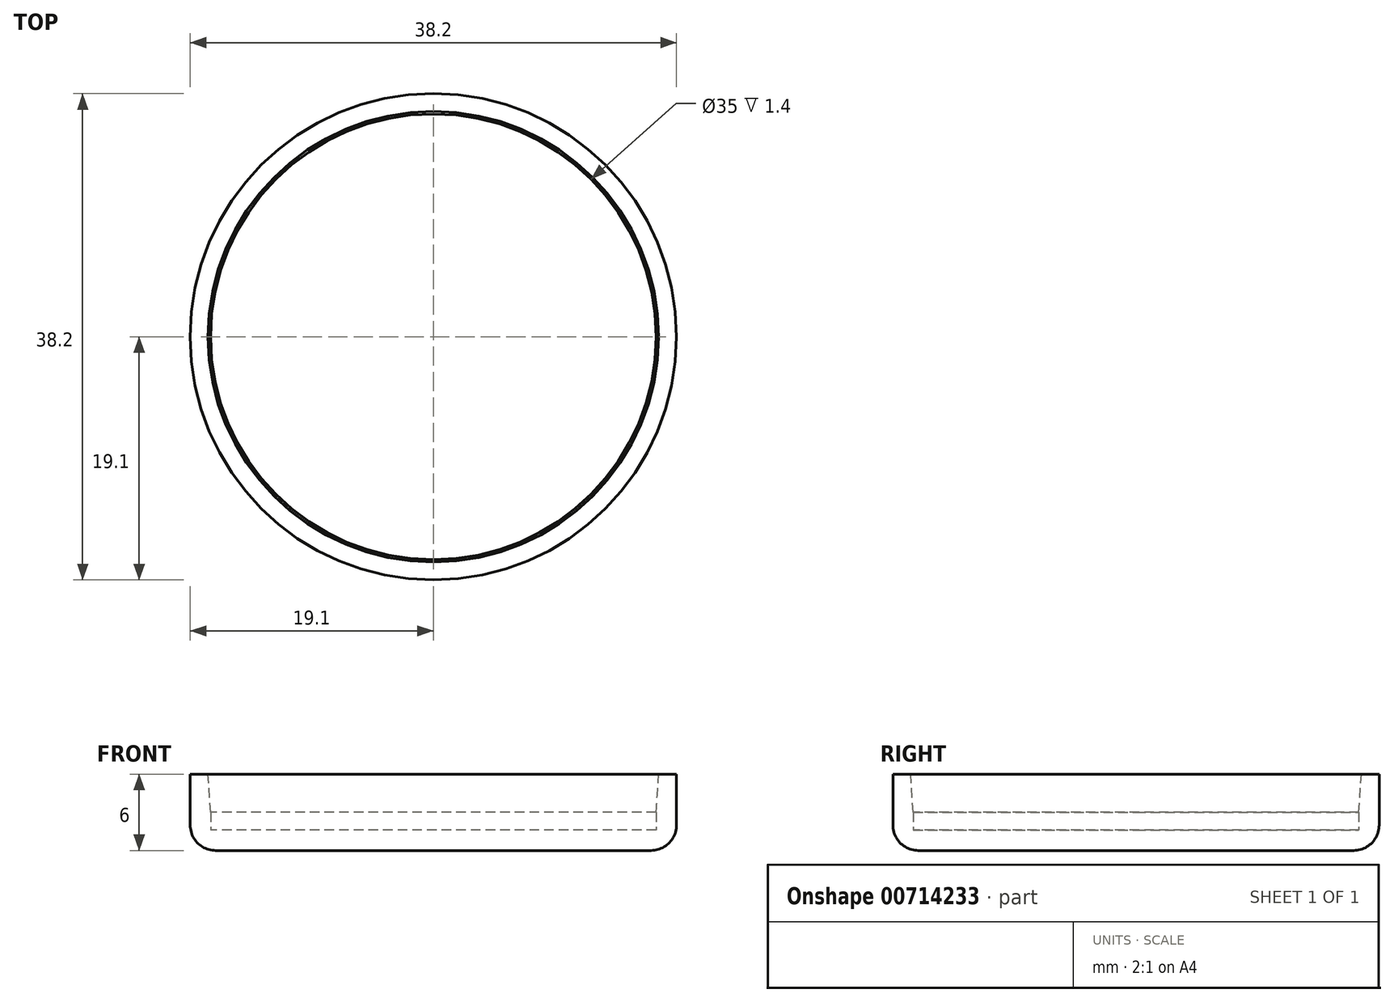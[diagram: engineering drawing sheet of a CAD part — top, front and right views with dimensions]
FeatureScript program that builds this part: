
annotation { "Feature Type Name" : "Feature", "Feature Type Description" : "" }
export const myFeature = defineFeature(function(context is Context, id is Id, definition is map)
    precondition{}
    {
        {
            var Q0;
            Q0=qCreatedBy(makeId("Top.planeOp"),FACE);
            var sketch = newSketch(context, id + "F0", { "sketchPlane" : qUnion([Q0])});
            skCircle(sketch, "E0", {"center": v(0, 0) * mm, "radius": 19.1 * mm});
            skCircle(sketch, "E1", {"center": v(0, 0) * mm, "radius": 17.5 * mm});
            skSolve(sketch);
        }
        {
            var Q0;
            Q0=makeQuery(id+"F0.imprint","IMPRINT",FACE,{"disambiguationData":[TD([[makeQuery(id+"F0.imprint","IMPRINT",EDGE,{"derivedFrom":sQuery(id+"F0.wireOp",EDGE,"E1")}),1.0]])]});
            extrude(context, id + "F1", {"entities" : qUnion([Q0]), "depth" : 1.6 * mm, "offsetDistance" : 25 * mm});
        }
        {
            var Q0;
            Q0=qSketchRegion(id+"F0",true);
            extrude(context, id + "F2", {"entities" : qUnion([Q0]), "operationType" : NewBodyOperationType.ADD, "depth" : 6 * mm, "offsetDistance" : 25 * mm});
        }
        {
            var Q0;
            Q0=makeQuery(id+"F2.opExtrude","CAP_EDGE",EDGE,{"disambiguationData":[OSD([sQuery(id+"F0.wireOp",EDGE,"E1")])],"isStart":false});
            chamfer(context, id + "F3", {"entities" : qUnion([Q0]), "chamferType" : ChamferType.TWO_OFFSETS, "width1" : 0.2 * mm, "oppositeDirection" : true, "width2" : 3 * mm});
        }
        {
            var Q0;
            Q0=makeQuery(id+"F2.opExtrude","CAP_EDGE",EDGE,{"disambiguationData":[OSD([sQuery(id+"F0.wireOp",EDGE,"E0")])],"isStart":true});
            fillet(context, id + "F4", {"entities" : qUnion([Q0]), "radius" : 2 * mm, "tangentPropagation" : true, "allowEdgeOverflow" : false});
        }
    });
